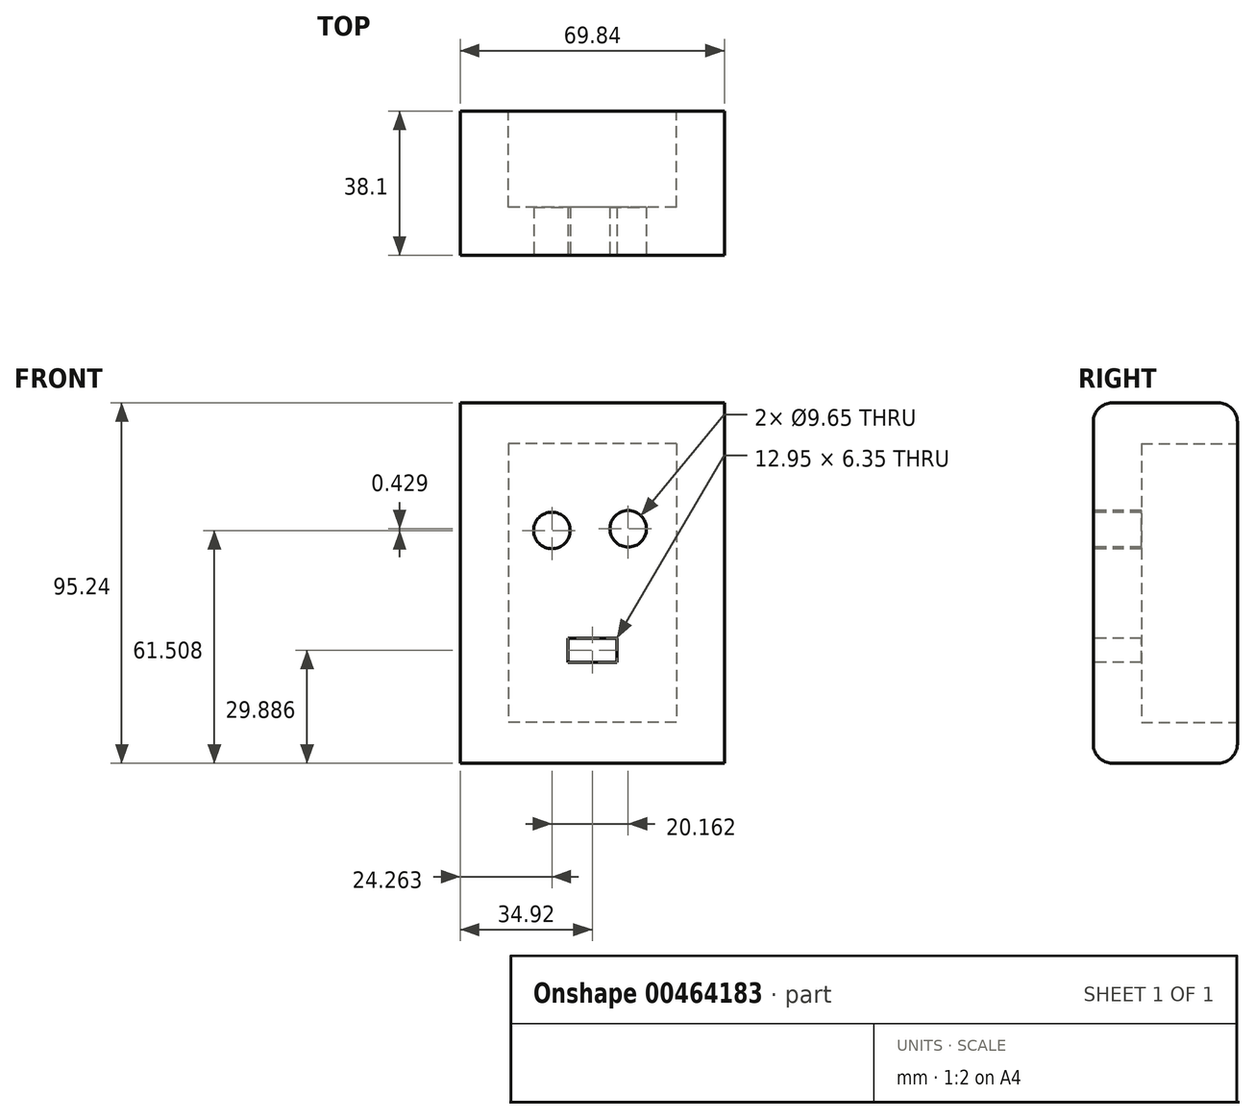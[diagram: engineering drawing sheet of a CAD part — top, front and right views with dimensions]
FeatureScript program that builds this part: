
annotation { "Feature Type Name" : "Feature", "Feature Type Description" : "" }
export const myFeature = defineFeature(function(context is Context, id is Id, definition is map)
    precondition{}
    {
        {
            var Q0;
            Q0=qCreatedBy(makeId("Front.planeOp"),FACE);
            var sketch = newSketch(context, id + "F0", { "sketchPlane" : qUnion([Q0])});
            skLineSegment(sketch, "E0.bottom", {"start": v(-34.92, 47.63) * mm, "end": v(34.93, 47.63) * mm});
            skLineSegment(sketch, "E0.top", {"start": v(-34.93, -47.63) * mm, "end": v(34.92, -47.63) * mm});
            skLineSegment(sketch, "E0.left", {"start": v(-34.92, 47.63) * mm, "end": v(-34.93, -47.62) * mm});
            skLineSegment(sketch, "E0.right", {"start": v(34.93, 47.62) * mm, "end": v(34.92, -47.63) * mm});
            skPoint(sketch, "E0.middle", {"position": v(0, 0) * mm});
            skSolve(sketch);
        }
        {
            var Q0;
            Q0 = qSketchRegion(id + "F0", true);
            extrude(context, id + "F1", {"entities" : qUnion([Q0]), "depth" : 38.1 * mm});
        }
        {
            var Q0;
            Q0=makeQuery(id+"F1.opExtrude","CAP_FACE",FACE,{"disambiguationData":[OSD([sQuery(id+"F0.wireOp",EDGE,"E0.bottom"),sQuery(id+"F0.wireOp",EDGE,"E0.top"),sQuery(id+"F0.wireOp",EDGE,"E0.left"),sQuery(id+"F0.wireOp",EDGE,"E0.right")])],"isStart":true});
            var sketch = newSketch(context, id + "F2", { "sketchPlane" : qUnion([Q0])});
            skLineSegment(sketch, "E1.bottom", {"start": v(-22.22, 36.83) * mm, "end": v(22.23, 36.83) * mm});
            skLineSegment(sketch, "E1.top", {"start": v(-22.23, -36.83) * mm, "end": v(22.22, -36.83) * mm});
            skLineSegment(sketch, "E1.left", {"start": v(-22.22, 36.83) * mm, "end": v(-22.23, -36.83) * mm});
            skLineSegment(sketch, "E1.right", {"start": v(22.23, 36.83) * mm, "end": v(22.22, -36.83) * mm});
            skPoint(sketch, "E1.middle", {"position": v(0, 0) * mm});
            skSolve(sketch);
        }
        {
            var Q0;
            Q0 = qSketchRegion(id + "F2", true);
            extrude(context, id + "F3", {"entities" : qUnion([Q0]), "operationType" : NewBodyOperationType.REMOVE, "oppositeDirection" : true, "depth" : 25.4 * mm});
        }
        {
            var Q0;
            Q0=makeQuery(id+"F1.opExtrude","CAP_EDGE",EDGE,{"disambiguationData":[OSD([sQuery(id+"F0.wireOp",EDGE,"E0.bottom")])],"isStart":false});
            var Q1;
            Q1=makeQuery(id+"F1.opExtrude","CAP_EDGE",EDGE,{"disambiguationData":[OSD([sQuery(id+"F0.wireOp",EDGE,"E0.bottom")])],"isStart":true});
            var Q2;
            Q2=makeQuery(id+"F1.opExtrude","CAP_EDGE",EDGE,{"disambiguationData":[OSD([sQuery(id+"F0.wireOp",EDGE,"E0.top")])],"isStart":false});
            var Q3;
            Q3=makeQuery(id+"F1.opExtrude","CAP_EDGE",EDGE,{"disambiguationData":[OSD([sQuery(id+"F0.wireOp",EDGE,"E0.top")])],"isStart":true});
            fillet(context, id + "F4", {"entities" : qUnion([Q0, Q1, Q2, Q3]), "radius" : 5.08 * mm, "tangentPropagation" : true, "allowEdgeOverflow" : false});
        }
        {
            var Q0;
            Q0=makeQuery(id+"F1.opExtrude","CAP_FACE",FACE,{"disambiguationData":[OSD([sQuery(id+"F0.wireOp",EDGE,"E0.bottom"),sQuery(id+"F0.wireOp",EDGE,"E0.top"),sQuery(id+"F0.wireOp",EDGE,"E0.left"),sQuery(id+"F0.wireOp",EDGE,"E0.right")])],"isStart":false});
            var sketch = newSketch(context, id + "F5", { "sketchPlane" : qUnion([Q0])});
            skCircle(sketch, "E2", {"center": v(-10.66, 13.89) * mm, "radius": 4.83 * mm});
            skCircle(sketch, "E3", {"center": v(9.5, 14.32) * mm, "radius": 4.83 * mm});
            skSolve(sketch);
        }
        {
            var Q0;
            Q0=makeQuery(id+"F5.imprint","IMPRINT",FACE,{"disambiguationData":[TD([[makeQuery(id+"F5.imprint","IMPRINT",EDGE,{"derivedFrom":sQuery(id+"F5.wireOp",EDGE,"E2")}),1.0]])]});
            var Q1;
            Q1=makeQuery(id+"F5.imprint","IMPRINT",FACE,{"disambiguationData":[TD([[makeQuery(id+"F5.imprint","IMPRINT",EDGE,{"derivedFrom":sQuery(id+"F5.wireOp",EDGE,"ceafb361-d695-487b-9dd0-287d78877f3b")}),1.0]])]});
            var Q2;
            Q2=makeQuery(id+"F5.imprint","IMPRINT",FACE,{"disambiguationData":[TD([[makeQuery(id+"F5.imprint","IMPRINT",EDGE,{"derivedFrom":sQuery(id+"F5.wireOp",EDGE,"E3")}),1.0]])]});
            extrude(context, id + "F6", {"entities" : qUnion([Q0, Q1, Q2]), "operationType" : NewBodyOperationType.REMOVE, "oppositeDirection" : true, "depth" : 12.7 * mm});
        }
        {
            var Q0;
            Q0=makeQuery(id+"F1.opExtrude","CAP_FACE",FACE,{"disambiguationData":[OSD([sQuery(id+"F0.wireOp",EDGE,"E0.bottom"),sQuery(id+"F0.wireOp",EDGE,"E0.top"),sQuery(id+"F0.wireOp",EDGE,"E0.left"),sQuery(id+"F0.wireOp",EDGE,"E0.right")])],"isStart":false});
            var sketch = newSketch(context, id + "F7", { "sketchPlane" : qUnion([Q0])});
            skLineSegment(sketch, "E4.bottom", {"start": v(6.48, -20.9) * mm, "end": v(-6.48, -20.9) * mm});
            skLineSegment(sketch, "E4.top", {"start": v(6.48, -14.56) * mm, "end": v(-6.48, -14.56) * mm});
            skLineSegment(sketch, "E4.left", {"start": v(6.48, -20.9) * mm, "end": v(6.48, -14.56) * mm});
            skLineSegment(sketch, "E4.right", {"start": v(-6.48, -20.9) * mm, "end": v(-6.48, -14.56) * mm});
            skPoint(sketch, "E4.middle", {"position": v(0, -17.73) * mm});
            skSolve(sketch);
        }
        {
            var Q0;
            Q0 = qSketchRegion(id + "F7", true);
            extrude(context, id + "F8", {"entities" : qUnion([Q0]), "operationType" : NewBodyOperationType.REMOVE, "oppositeDirection" : true, "depth" : 12.7 * mm});
        }
    });
